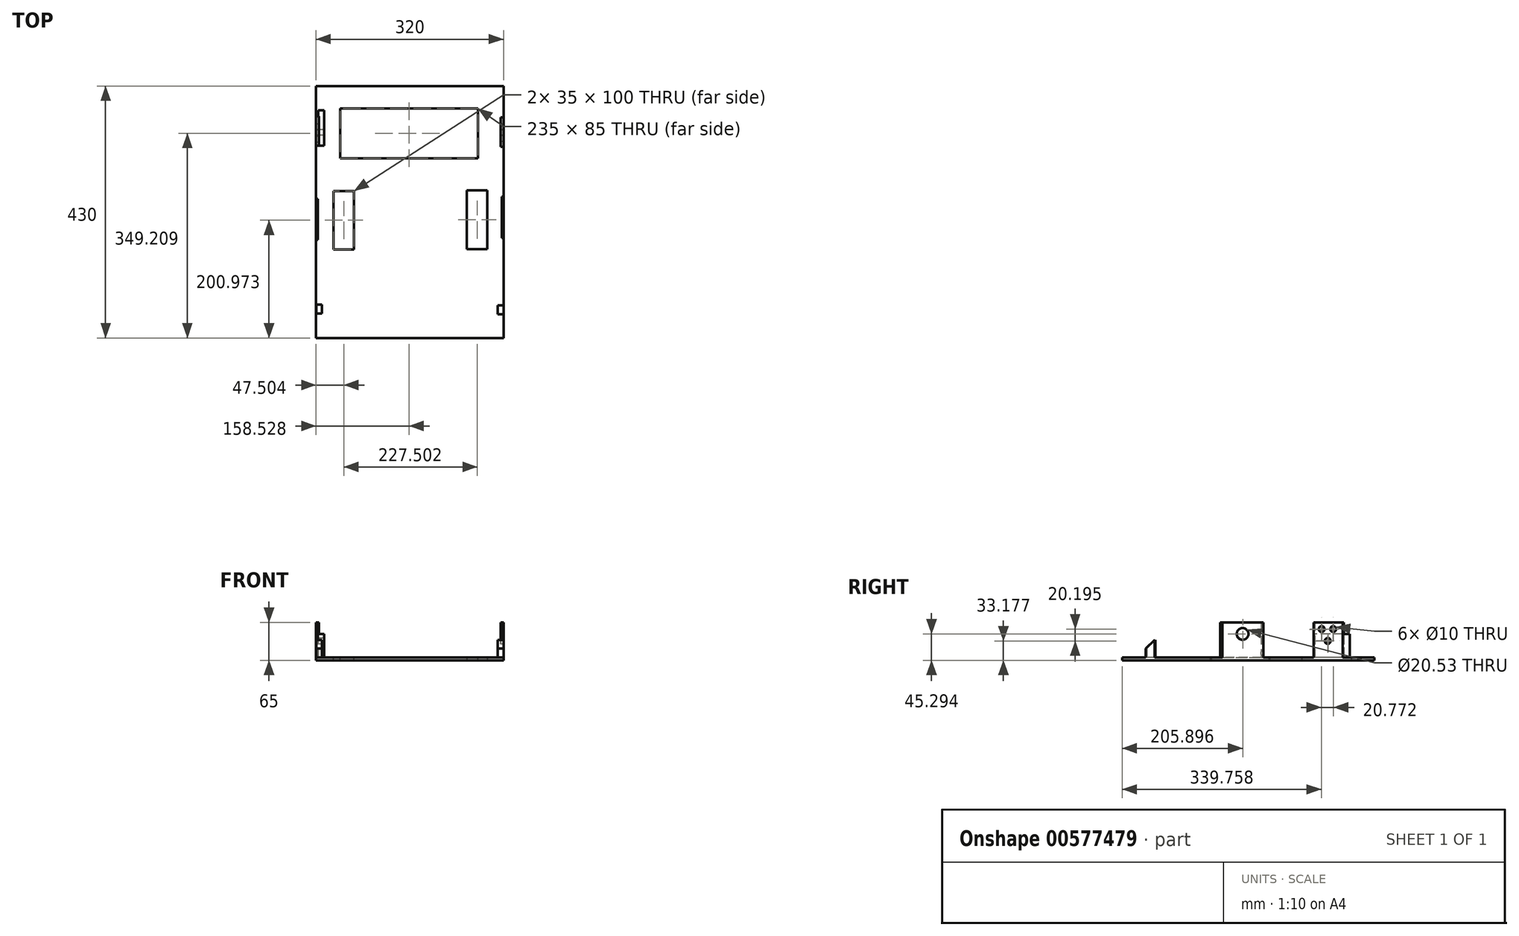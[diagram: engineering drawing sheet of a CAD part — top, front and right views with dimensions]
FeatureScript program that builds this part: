
annotation { "Feature Type Name" : "Feature", "Feature Type Description" : "" }
export const myFeature = defineFeature(function(context is Context, id is Id, definition is map)
    precondition{}
    {
        {
            var Q0;
            Q0=qCreatedBy(makeId("Top.planeOp"),FACE);
            var sketch = newSketch(context, id + "F0", { "sketchPlane" : qUnion([Q0])});
            skLineSegment(sketch, "E0.bottom", {"start": v(112.71, -29.67) * mm, "end": v(-207.29, -29.67) * mm});
            skLineSegment(sketch, "E0.top", {"start": v(112.71, 400.33) * mm, "end": v(-207.29, 400.33) * mm});
            skLineSegment(sketch, "E0.left", {"start": v(112.71, -29.67) * mm, "end": v(112.71, 400.33) * mm});
            skLineSegment(sketch, "E0.right", {"start": v(-207.29, -29.67) * mm, "end": v(-207.29, 400.33) * mm});
            skPoint(sketch, "E0.middle", {"position": v(-47.29, 185.33) * mm});
            skSolve(sketch);
        }
        {
            var Q0;
            Q0=makeQuery(id+"F0.imprint","IMPRINT",FACE,{"disambiguationData":[TD([[makeQuery(id+"F0.imprint","IMPRINT",EDGE,{"derivedFrom":sQuery(id+"F0.wireOp",EDGE,"E0.bottom")}),-1.0]])]});
            extrude(context, id + "F1", {"entities" : qUnion([Q0]), "depth" : 5 * mm});
        }
        {
            var Q0;
            Q0=makeQuery(id+"F1.opExtrude","CAP_FACE",FACE,{"disambiguationData":[OSD([sQuery(id+"F0.wireOp",EDGE,"E0.bottom"),sQuery(id+"F0.wireOp",EDGE,"E0.top"),sQuery(id+"F0.wireOp",EDGE,"E0.left"),sQuery(id+"F0.wireOp",EDGE,"E0.right")])],"isStart":false});
            var sketch = newSketch(context, id + "F2", { "sketchPlane" : qUnion([Q0])});
            skLineSegment(sketch, "E1.bottom", {"start": v(-142.29, 121.3) * mm, "end": v(-177.29, 121.3) * mm});
            skLineSegment(sketch, "E1.top", {"start": v(-142.29, 221.3) * mm, "end": v(-177.29, 221.3) * mm});
            skLineSegment(sketch, "E1.left", {"start": v(-142.29, 121.3) * mm, "end": v(-142.29, 221.3) * mm});
            skLineSegment(sketch, "E1.right", {"start": v(-177.29, 121.3) * mm, "end": v(-177.29, 221.3) * mm});
            skPoint(sketch, "E1.middle", {"position": v(-159.79, 171.3) * mm});
            skSolve(sketch);
        }
        {
            var Q0;
            Q0=qSketchRegion(id+"F2",true);
            extrude(context, id + "F3", {"entities" : qUnion([Q0]), "operationType" : NewBodyOperationType.REMOVE, "oppositeDirection" : true, "depth" : 5 * mm, "offsetDistance" : 25 * mm});
        }
        {
            var Q0;
            Q0=makeQuery(id+"F1.opExtrude","CAP_FACE",FACE,{"disambiguationData":[OSD([sQuery(id+"F0.wireOp",EDGE,"E0.bottom"),sQuery(id+"F0.wireOp",EDGE,"E0.top"),sQuery(id+"F0.wireOp",EDGE,"E0.left"),sQuery(id+"F0.wireOp",EDGE,"E0.right")])],"isStart":true});
            var sketch = newSketch(context, id + "F4", { "sketchPlane" : qUnion([Q0])});
            skLineSegment(sketch, "E2.bottom", {"start": v(50.22, -122.21) * mm, "end": v(85.22, -122.21) * mm});
            skLineSegment(sketch, "E2.top", {"start": v(50.22, -222.21) * mm, "end": v(85.22, -222.21) * mm});
            skLineSegment(sketch, "E2.left", {"start": v(50.22, -122.21) * mm, "end": v(50.22, -222.21) * mm});
            skLineSegment(sketch, "E2.right", {"start": v(85.22, -122.21) * mm, "end": v(85.22, -222.21) * mm});
            skPoint(sketch, "E2.middle", {"position": v(67.72, -172.21) * mm});
            skSolve(sketch);
        }
        {
            var Q0;
            Q0=qSketchRegion(id+"F4",true);
            extrude(context, id + "F5", {"entities" : qUnion([Q0]), "operationType" : NewBodyOperationType.REMOVE, "oppositeDirection" : true, "depth" : 5 * mm});
        }
        {
            var Q0;
            Q0=makeQuery(id+"F1.opExtrude","CAP_FACE",FACE,{"disambiguationData":[OSD([sQuery(id+"F0.wireOp",EDGE,"E0.bottom"),sQuery(id+"F0.wireOp",EDGE,"E0.top"),sQuery(id+"F0.wireOp",EDGE,"E0.left"),sQuery(id+"F0.wireOp",EDGE,"E0.right")])],"isStart":false});
            var sketch = newSketch(context, id + "F6", { "sketchPlane" : qUnion([Q0])});
            skLineSegment(sketch, "E3.bottom", {"start": v(-166.26, 362.04) * mm, "end": v(68.74, 362.04) * mm});
            skLineSegment(sketch, "E3.top", {"start": v(-166.26, 277.04) * mm, "end": v(68.74, 277.04) * mm});
            skLineSegment(sketch, "E3.left", {"start": v(-166.26, 362.04) * mm, "end": v(-166.26, 277.04) * mm});
            skLineSegment(sketch, "E3.right", {"start": v(68.74, 362.04) * mm, "end": v(68.74, 277.04) * mm});
            skLineSegment(sketch, "E4.bottom", {"start": v(-48.76, 277.04) * mm, "end": v(-65.01, 277.04) * mm});
            skLineSegment(sketch, "E4.top", {"start": v(-48.76, 277.04) * mm, "end": v(-65.01, 277.04) * mm});
            skLineSegment(sketch, "E4.left", {"start": v(-48.76, 277.04) * mm, "end": v(-48.76, 277.04) * mm});
            skLineSegment(sketch, "E4.right", {"start": v(-65.01, 277.04) * mm, "end": v(-65.01, 277.04) * mm});
            skSolve(sketch);
        }
        {
            var Q0;
            Q0=qSketchRegion(id+"F6",true);
            extrude(context, id + "F7", {"entities" : qUnion([Q0]), "operationType" : NewBodyOperationType.REMOVE, "oppositeDirection" : true, "depth" : 5 * mm});
        }
        {
            var Q0;
            Q0=makeQuery(id+"F1.opExtrude","CAP_FACE",FACE,{"disambiguationData":[OSD([sQuery(id+"F0.wireOp",EDGE,"E0.bottom"),sQuery(id+"F0.wireOp",EDGE,"E0.top"),sQuery(id+"F0.wireOp",EDGE,"E0.left"),sQuery(id+"F0.wireOp",EDGE,"E0.right")])],"isStart":false});
            var sketch = newSketch(context, id + "F8", { "sketchPlane" : qUnion([Q0])});
            skLineSegment(sketch, "E5.bottom", {"start": v(-207.29, 207.67) * mm, "end": v(-204.29, 207.67) * mm});
            skLineSegment(sketch, "E5.top", {"start": v(-207.29, 137.67) * mm, "end": v(-204.29, 137.67) * mm});
            skLineSegment(sketch, "E5.left", {"start": v(-207.29, 207.67) * mm, "end": v(-207.29, 137.67) * mm});
            skLineSegment(sketch, "E5.right", {"start": v(-204.29, 207.67) * mm, "end": v(-204.29, 137.67) * mm});
            skSolve(sketch);
        }
        {
            var Q0;
            Q0=qSketchRegion(id+"F8",true);
            extrude(context, id + "F9", {"entities" : qUnion([Q0]), "operationType" : NewBodyOperationType.ADD, "depth" : 60 * mm});
        }
        {
            var Q0;
            Q0=makeQuery(id+"F1.opExtrude","CAP_FACE",FACE,{"disambiguationData":[OSD([sQuery(id+"F0.wireOp",EDGE,"E0.bottom"),sQuery(id+"F0.wireOp",EDGE,"E0.top"),sQuery(id+"F0.wireOp",EDGE,"E0.left"),sQuery(id+"F0.wireOp",EDGE,"E0.right")])],"isStart":false});
            var sketch = newSketch(context, id + "F10", { "sketchPlane" : qUnion([Q0])});
            skLineSegment(sketch, "E6.bottom", {"start": v(112.71, 211.3) * mm, "end": v(109.71, 211.3) * mm});
            skLineSegment(sketch, "E6.top", {"start": v(112.71, 141.3) * mm, "end": v(109.71, 141.3) * mm});
            skLineSegment(sketch, "E6.left", {"start": v(112.71, 211.3) * mm, "end": v(112.71, 141.3) * mm});
            skLineSegment(sketch, "E6.right", {"start": v(109.71, 211.3) * mm, "end": v(109.71, 141.3) * mm});
            skSolve(sketch);
        }
        {
            var Q0;
            Q0=qSketchRegion(id+"F10",true);
            extrude(context, id + "F11", {"entities" : qUnion([Q0]), "operationType" : NewBodyOperationType.ADD, "depth" : 60 * mm});
        }
        {
            var Q0;
            Q0=makeQuery(id+"F1.opExtrude","CAP_FACE",FACE,{"disambiguationData":[OSD([sQuery(id+"F0.wireOp",EDGE,"E0.bottom"),sQuery(id+"F0.wireOp",EDGE,"E0.top"),sQuery(id+"F0.wireOp",EDGE,"E0.left"),sQuery(id+"F0.wireOp",EDGE,"E0.right")])],"isStart":false});
            var sketch = newSketch(context, id + "F12", { "sketchPlane" : qUnion([Q0])});
            skLineSegment(sketch, "E7.bottom", {"start": v(-207.29, 348.58) * mm, "end": v(-202.29, 348.58) * mm});
            skLineSegment(sketch, "E7.top", {"start": v(-207.29, 298.58) * mm, "end": v(-202.29, 298.58) * mm});
            skLineSegment(sketch, "E7.left", {"start": v(-207.29, 348.58) * mm, "end": v(-207.29, 298.58) * mm});
            skLineSegment(sketch, "E7.right", {"start": v(-202.29, 348.58) * mm, "end": v(-202.29, 298.58) * mm});
            skSolve(sketch);
        }
        {
            var Q0;
            Q0=qSketchRegion(id+"F12",true);
            extrude(context, id + "F13", {"entities" : qUnion([Q0]), "operationType" : NewBodyOperationType.ADD, "depth" : 60 * mm, "offsetDistance" : 25 * mm});
        }
        {
            var Q0;
            Q0=makeQuery(id+"F1.opExtrude","CAP_FACE",FACE,{"disambiguationData":[OSD([sQuery(id+"F0.wireOp",EDGE,"E0.bottom"),sQuery(id+"F0.wireOp",EDGE,"E0.top"),sQuery(id+"F0.wireOp",EDGE,"E0.left"),sQuery(id+"F0.wireOp",EDGE,"E0.right")])],"isStart":false});
            var sketch = newSketch(context, id + "F14", { "sketchPlane" : qUnion([Q0])});
            skLineSegment(sketch, "E8.bottom", {"start": v(112.71, 346.76) * mm, "end": v(107.71, 346.76) * mm});
            skLineSegment(sketch, "E8.top", {"start": v(112.71, 296.76) * mm, "end": v(107.71, 296.76) * mm});
            skLineSegment(sketch, "E8.left", {"start": v(112.71, 346.76) * mm, "end": v(112.71, 296.76) * mm});
            skLineSegment(sketch, "E8.right", {"start": v(107.71, 346.76) * mm, "end": v(107.71, 296.76) * mm});
            skSolve(sketch);
        }
        {
            var Q0;
            Q0=qSketchRegion(id+"F14",true);
            extrude(context, id + "F15", {"entities" : qUnion([Q0]), "operationType" : NewBodyOperationType.ADD, "depth" : 60 * mm});
        }
        {
            var Q0;
            Q0=qCreatedBy(makeId("Right.planeOp"),FACE);
            var sketch = newSketch(context, id + "F16", { "sketchPlane" : qUnion([Q0])});
            skCircle(sketch, "E9", {"center": v(175.78, 45.06) * mm, "radius": 10 * mm});
            skSolve(sketch);
        }
        {
            var Q0;
            Q0=qSketchRegion(id+"F16",true);
            extrude(context, id + "F17", {"entities" : qUnion([Q0]), "operationType" : NewBodyOperationType.REMOVE, "depth" : 120 * mm});
        }
        {
            var Q0;
            Q0=qCreatedBy(makeId("Right.planeOp"),FACE);
            var sketch = newSketch(context, id + "F18", { "sketchPlane" : qUnion([Q0])});
            skCircle(sketch, "E10", {"center": v(176.23, 45.3) * mm, "radius": 10.26 * mm});
            skSolve(sketch);
        }
        {
            var Q0;
            Q0=qSketchRegion(id+"F18",true);
            extrude(context, id + "F19", {"entities" : qUnion([Q0]), "operationType" : NewBodyOperationType.REMOVE, "oppositeDirection" : true, "depth" : 240 * mm});
        }
        {
            var Q0;
            Q0=makeQuery(id+"F1.opExtrude","CAP_FACE",FACE,{"disambiguationData":[OSD([sQuery(id+"F0.wireOp",EDGE,"E0.bottom"),sQuery(id+"F0.wireOp",EDGE,"E0.top"),sQuery(id+"F0.wireOp",EDGE,"E0.left"),sQuery(id+"F0.wireOp",EDGE,"E0.right")])],"isStart":false});
            var sketch = newSketch(context, id + "F20", { "sketchPlane" : qUnion([Q0])});
            skLineSegment(sketch, "E11.bottom", {"start": v(102.71, 25.85) * mm, "end": v(112.71, 25.85) * mm});
            skLineSegment(sketch, "E11.top", {"start": v(102.71, 10.85) * mm, "end": v(112.71, 10.85) * mm});
            skLineSegment(sketch, "E11.left", {"start": v(102.71, 25.85) * mm, "end": v(102.71, 10.85) * mm});
            skLineSegment(sketch, "E11.right", {"start": v(112.71, 25.85) * mm, "end": v(112.71, 10.85) * mm});
            skSolve(sketch);
        }
        {
            var Q0;
            Q0=qSketchRegion(id+"F20",true);
            extrude(context, id + "F21", {"entities" : qUnion([Q0]), "operationType" : NewBodyOperationType.ADD, "depth" : 30 * mm});
        }
        {
            var Q0;
            Q0=makeQuery(id+"F21.opExtrude","CAP_EDGE",EDGE,{"disambiguationData":[OSD([sQuery(id+"F20.wireOp",EDGE,"E11.top")])],"isStart":false});
            chamfer(context, id + "F22", {"entities" : qUnion([Q0]), "width" : 15 * mm, "tangentPropagation" : true});
        }
        {
            var Q0;
            {var subQ14=sQuery(id+"F20.wireOp",EDGE,"E11.bottom");Q0=makeQuery(id+"F20.imprint","IMPRINT",FACE,{"disambiguationData":[TD([[makeQuery(id+"F20.imprint","IMPRINT",EDGE,{"derivedFrom":subQ14}),1.0]])]});}
            var sketch = newSketch(context, id + "F23", { "sketchPlane" : qUnion([Q0])});
            skLineSegment(sketch, "E12.bottom", {"start": v(-206.83, 27.2) * mm, "end": v(-196.83, 27.2) * mm});
            skLineSegment(sketch, "E12.top", {"start": v(-206.83, 12.2) * mm, "end": v(-196.83, 12.2) * mm});
            skLineSegment(sketch, "E12.left", {"start": v(-206.83, 27.2) * mm, "end": v(-206.83, 12.2) * mm});
            skLineSegment(sketch, "E12.right", {"start": v(-196.83, 27.2) * mm, "end": v(-196.83, 12.2) * mm});
            skSolve(sketch);
        }
        {
            var Q0;
            Q0=qSketchRegion(id+"F23",true);
            extrude(context, id + "F24", {"entities" : qUnion([Q0]), "operationType" : NewBodyOperationType.ADD, "depth" : 30 * mm});
        }
        {
            var Q0;
            Q0=makeQuery(id+"F24.opExtrude","CAP_EDGE",EDGE,{"disambiguationData":[OSD([sQuery(id+"F23.wireOp",EDGE,"E12.top")])],"isStart":false});
            chamfer(context, id + "F25", {"entities" : qUnion([Q0]), "width" : 15 * mm, "tangentPropagation" : true});
        }
        {
            var Q0;
            Q0=makeQuery(id+"F1.opExtrude","CAP_FACE",FACE,{"disambiguationData":[OSD([sQuery(id+"F0.wireOp",EDGE,"E0.bottom"),sQuery(id+"F0.wireOp",EDGE,"E0.top"),sQuery(id+"F0.wireOp",EDGE,"E0.left"),sQuery(id+"F0.wireOp",EDGE,"E0.right")])],"isStart":false});
            var sketch = newSketch(context, id + "F26", { "sketchPlane" : qUnion([Q0])});
            skLineSegment(sketch, "E13.bottom", {"start": v(-203.2, 358.58) * mm, "end": v(-193.2, 358.58) * mm});
            skLineSegment(sketch, "E13.top", {"start": v(-203.2, 298.58) * mm, "end": v(-193.2, 298.58) * mm});
            skLineSegment(sketch, "E13.left", {"start": v(-203.2, 358.58) * mm, "end": v(-203.2, 298.58) * mm});
            skLineSegment(sketch, "E13.right", {"start": v(-193.2, 358.58) * mm, "end": v(-193.2, 298.58) * mm});
            skSolve(sketch);
        }
        {
            var Q0;
            Q0=qSketchRegion(id+"F26",true);
            extrude(context, id + "F27", {"entities" : qUnion([Q0]), "operationType" : NewBodyOperationType.ADD, "depth" : 40 * mm, "offsetDistance" : 25 * mm});
        }
        {
            var Q0;
            Q0=qCreatedBy(makeId("Right.planeOp"),FACE);
            var sketch = newSketch(context, id + "F28", { "sketchPlane" : qUnion([Q0])});
            skCircle(sketch, "E14", {"center": v(310.66, 53.37) * mm, "radius": 5 * mm});
            skSolve(sketch);
        }
        {
            var Q0;
            Q0=qSketchRegion(id+"F28",true);
            extrude(context, id + "F29", {"entities" : qUnion([Q0]), "operationType" : NewBodyOperationType.REMOVE, "depth" : 240 * mm, "offsetDistance" : 25 * mm});
        }
        {
            var Q0;
            Q0=qCreatedBy(makeId("Right.planeOp"),FACE);
            var sketch = newSketch(context, id + "F30", { "sketchPlane" : qUnion([Q0])});
            skCircle(sketch, "E15", {"center": v(330.28, 53.37) * mm, "radius": 5 * mm});
            skSolve(sketch);
        }
        {
            var Q0;
            Q0=qSketchRegion(id+"F30",true);
            extrude(context, id + "F31", {"entities" : qUnion([Q0]), "operationType" : NewBodyOperationType.REMOVE, "depth" : 240 * mm, "offsetDistance" : 25 * mm});
        }
        {
            var Q0;
            Q0=qCreatedBy(makeId("Right.planeOp"),FACE);
            var sketch = newSketch(context, id + "F32", { "sketchPlane" : qUnion([Q0])});
            skCircle(sketch, "E16", {"center": v(321.05, 33.18) * mm, "radius": 5 * mm});
            skSolve(sketch);
        }
        {
            var Q0;
            Q0=qSketchRegion(id+"F32",true);
            extrude(context, id + "F33", {"entities" : qUnion([Q0]), "operationType" : NewBodyOperationType.REMOVE, "depth" : 250 * mm, "offsetDistance" : 25 * mm});
        }
        {
            var Q0;
            Q0=qCreatedBy(makeId("Right.planeOp"),FACE);
            var sketch = newSketch(context, id + "F34", { "sketchPlane" : qUnion([Q0])});
            skCircle(sketch, "E17", {"center": v(310.09, 52.8) * mm, "radius": 5 * mm});
            skSolve(sketch);
        }
        {
            var Q0;
            Q0=qSketchRegion(id+"F34",true);
            extrude(context, id + "F35", {"entities" : qUnion([Q0]), "operationType" : NewBodyOperationType.REMOVE, "oppositeDirection" : true, "depth" : 300 * mm, "offsetDistance" : 25 * mm});
        }
        {
            var Q0;
            Q0=qCreatedBy(makeId("Right.planeOp"),FACE);
            var sketch = newSketch(context, id + "F36", { "sketchPlane" : qUnion([Q0])});
            skCircle(sketch, "E18", {"center": v(330.86, 53.37) * mm, "radius": 5 * mm});
            skSolve(sketch);
        }
        {
            var Q0;
            Q0=qSketchRegion(id+"F36",true);
            extrude(context, id + "F37", {"entities" : qUnion([Q0]), "operationType" : NewBodyOperationType.REMOVE, "oppositeDirection" : true, "depth" : 300 * mm, "offsetDistance" : 25 * mm});
        }
        {
            var Q0;
            Q0=qCreatedBy(makeId("Right.planeOp"),FACE);
            var sketch = newSketch(context, id + "F38", { "sketchPlane" : qUnion([Q0])});
            skCircle(sketch, "E19", {"center": v(321.63, 33.75) * mm, "radius": 5 * mm});
            skSolve(sketch);
        }
        {
            var Q0;
            Q0=qSketchRegion(id+"F38",true);
            extrude(context, id + "F39", {"entities" : qUnion([Q0]), "operationType" : NewBodyOperationType.REMOVE, "oppositeDirection" : true, "depth" : 300 * mm, "offsetDistance" : 25 * mm});
        }
        {
            var Q0;
            Q0=qCreatedBy(makeId("Right.planeOp"),FACE);
            var sketch = newSketch(context, id + "F40", { "sketchPlane" : qUnion([Q0])});
            skCircle(sketch, "E20", {"center": v(228, 27.1) * mm, "radius": 10 * mm});
            skSolve(sketch);
        }
        {
            var Q0;
            Q0=qSketchRegion(id+"F40",true);
            extrude(context, id + "F41", {"entities" : qUnion([Q0]), "operationType" : NewBodyOperationType.REMOVE, "endBound" : BoundingType.THROUGH_ALL, "oppositeDirection" : true, "depth" : 40 * mm, "offsetDistance" : 25 * mm});
        }
        {
            var Q0;
            Q0=qCreatedBy(makeId("Right.planeOp"),FACE);
            var sketch = newSketch(context, id + "F42", { "sketchPlane" : qUnion([Q0])});
            skCircle(sketch, "E21", {"center": v(241.43, 41.83) * mm, "radius": 5 * mm});
            skSolve(sketch);
        }
        {
            var Q0;
            Q0=qSketchRegion(id+"F42",true);
            extrude(context, id + "F43", {"entities" : qUnion([Q0]), "operationType" : NewBodyOperationType.REMOVE, "endBound" : BoundingType.THROUGH_ALL, "oppositeDirection" : true, "depth" : 25 * mm, "offsetDistance" : 25 * mm});
        }
        {
            var Q0;
            Q0=qCreatedBy(makeId("Right.planeOp"),FACE);
            var sketch = newSketch(context, id + "F44", { "sketchPlane" : qUnion([Q0])});
            skCircle(sketch, "E22", {"center": v(240.85, 12.98) * mm, "radius": 5 * mm});
            skSolve(sketch);
        }
        {
            var Q0;
            Q0=qSketchRegion(id+"F44",true);
            extrude(context, id + "F45", {"entities" : qUnion([Q0]), "operationType" : NewBodyOperationType.REMOVE, "endBound" : BoundingType.THROUGH_ALL, "oppositeDirection" : true, "depth" : 25 * mm, "offsetDistance" : 25 * mm});
        }
        {
            var Q0;
            Q0=qCreatedBy(makeId("Right.planeOp"),FACE);
            var sketch = newSketch(context, id + "F46", { "sketchPlane" : qUnion([Q0])});
            skCircle(sketch, "E23", {"center": v(213.08, 41.62) * mm, "radius": 5 * mm});
            skSolve(sketch);
        }
        {
            var Q0;
            Q0=qSketchRegion(id+"F46",true);
            extrude(context, id + "F47", {"entities" : qUnion([Q0]), "operationType" : NewBodyOperationType.REMOVE, "endBound" : BoundingType.THROUGH_ALL, "oppositeDirection" : true, "depth" : 25 * mm, "offsetDistance" : 25 * mm});
        }
        {
            var Q0;
            Q0=qCreatedBy(makeId("Right.planeOp"),FACE);
            var sketch = newSketch(context, id + "F48", { "sketchPlane" : qUnion([Q0])});
            skCircle(sketch, "E24", {"center": v(211.74, 12.1) * mm, "radius": 5 * mm});
            skSolve(sketch);
        }
        {
            var Q0;
            Q0=qSketchRegion(id+"F48",true);
            extrude(context, id + "F49", {"entities" : qUnion([Q0]), "operationType" : NewBodyOperationType.REMOVE, "endBound" : BoundingType.THROUGH_ALL, "oppositeDirection" : true, "depth" : 25 * mm, "offsetDistance" : 25 * mm});
        }
    });
